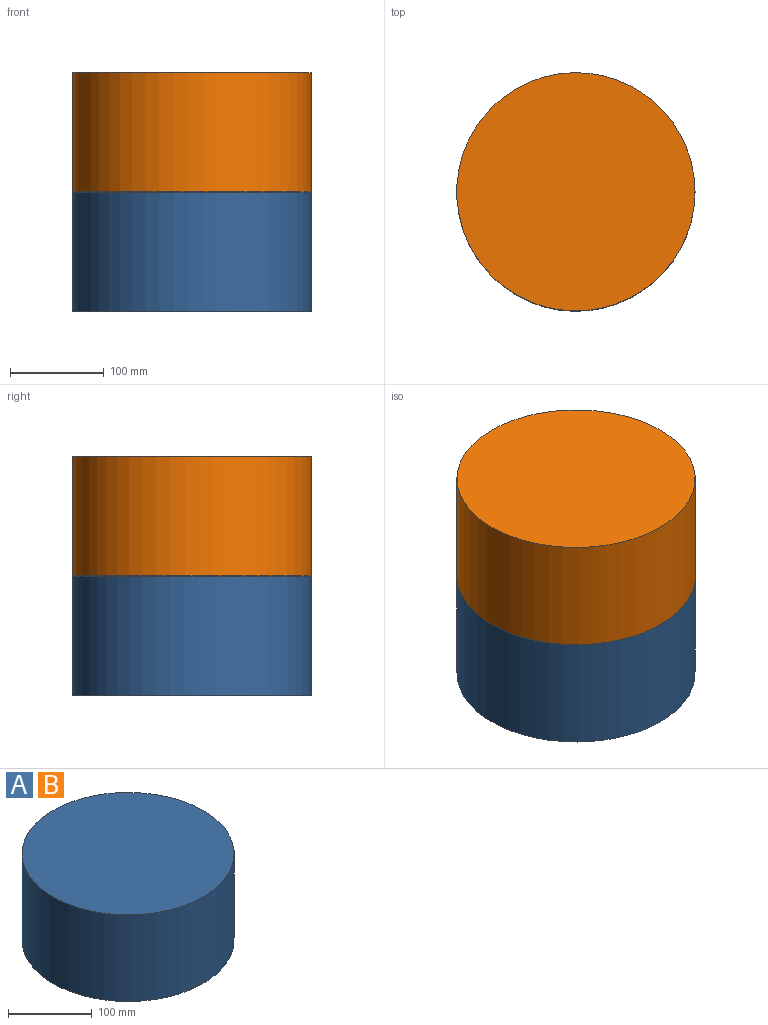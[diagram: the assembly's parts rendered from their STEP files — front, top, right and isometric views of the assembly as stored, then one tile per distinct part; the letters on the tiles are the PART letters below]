
ASSEMBLY  parts=2 mates=1
PART A: 3 faces, bbox 254x254x127 mm
  f0: cylinder r=127mm len=254mm, axis (0,0,1), area 101341.5mm2, adj f1,f2
  f1: plane 254x254mm, normal (0,0,-1), area 50670.7mm2, adj f0
  f2: plane 254x254mm, normal (0,0,1), area 50670.7mm2, adj f0
PART B: same geometry as A
PLACE A t=(53.85,4.91,-53.69)mm
PLACE B rot(axis=(1,0,0),180deg) t=(53.85,4.91,112.39)mm
MATE fastened B.f0 <-> A.f0  axis (0,0,-1) through (30.39,4.91,29.35)mm
